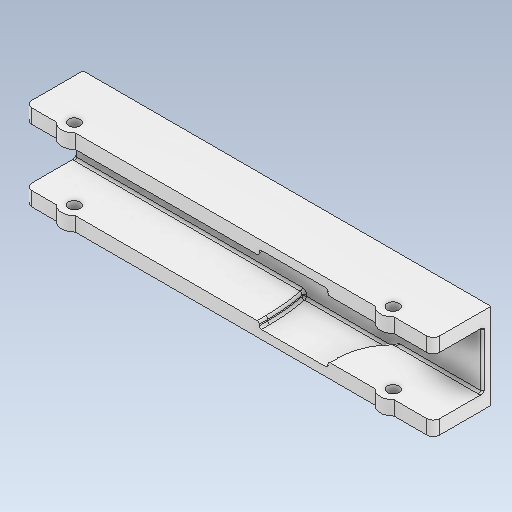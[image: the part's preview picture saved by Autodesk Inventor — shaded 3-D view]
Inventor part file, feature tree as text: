
AUTODESK INVENTOR PART (.ipt)
format: ipt  version: 2021 (Build 250183000, 183)  size: 329,216 bytes
history: native  units: mm
features: extrude x9, sketch x8, fillet x2, hole x1
ambient origin geometry x8: Origin, YZ Plane, XZ Plane, XY Plane, X Axis, Y Axis, Z Axis, Center Point
bodies: Solid1 (feature_tree)
feature tree (20):
  sketch  "Sketch1"  dims[d1=4.0mm d2=110.0mm]
  extrude  "Extrusion1"  Depth=110.0mm
  extrude  "Extrusion3"  Depth=40.4mm
  hole  "Hole1"  [1 undecoded]
  sketch  "Sketch6"  dims[d6=4.0mm d7=0.0mm d29=150.0mm]
  extrude  "Extrusion4"  Depth=19.15mm
  extrude  "Extrusion5"  TaperAngle=180.0deg  [1 undecoded]
  fillet  "Fillet1"  [1 undecoded]
  fillet  "Fillet2"  Radius=23.15mm
  extrude  "Extrusion6"  Depth=1.0mm
  extrude  "Extrusion7"  Depth=1.0mm
  extrude  "Extrusion8"  Depth=1.0mm
  extrude  "Extrusion9"  Depth=1.0mm
  extrude  "Extrusion10"  Depth=1.0mm
  sketch  "Sketch5"  dims[d3=40.4mm d5=82.0mm]
  sketch  "Sketch7"  dims[d31=23.15mm d32=0.0mm d33=19.15mm]
  sketch  "Sketch8"  dims[d34=19.15mm]
  sketch  "Sketch9"  dims[d35=5.5mm d36=6.0mm d37=4.0mm d38=2.0mm d39=90.0deg d40=8.0mm d41=0.0mm d42=180.0deg d43=0.0mm d44=23.15mm d45=0.0mm]
  sketch  "Sketch10"  dims[d46=23.15mm d47=0.0mm d48=1.0mm]
  sketch  "Sketch11"  dims[d49=3.0mm d50=87.57mm d51=4.0mm d52=4.0mm d53=4.0mm d54=3.0mm d55=1.0mm d56=3.0mm d57=1.0mm d58=0.0mm d59=0.0mm d60=12.0mm d61=23.15mm d62=0.0mm d63=12.0mm d64=23.15mm d65=0.0mm d66=12.0mm d67=23.15mm d68=0.0mm d69=12.0mm d70=23.15mm d71=0.0mm]
note: 3 required parameter values undecoded (feature->parameter linkage not recoverable at this tier; creation-order binding heuristic only, values carry confidence <= 0.55)
